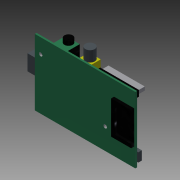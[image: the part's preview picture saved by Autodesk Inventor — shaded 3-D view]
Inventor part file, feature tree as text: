
AUTODESK INVENTOR PART (.ipt)
format: ipt  version: 2014 (Build 180170000, 170)  size: 240,128 bytes
history: native  units: mm
features: extrude x14, sketch x14
ambient origin geometry x8: Origin, YZ Plane, XZ Plane, XY Plane, X Axis, Y Axis, Z Axis, Center Point
bodies: Volumenkörper1 (feature_tree)
feature tree (28):
  extrude  "Extrusion1"  Depth=56.0mm
  extrude  "Extrusion2"  Depth=21.0mm
  extrude  "Extrusion3"  Depth=1.2mm
  extrude  "Extrusion4"  Depth=7.7mm
  extrude  "Extrusion5"  Depth=13.2mm
  extrude  "Extrusion6"  Depth=1.0mm
  extrude  "Extrusion7"  Depth=11.8mm
  extrude  "Extrusion8"  Depth=5.5mm TaperAngle=0.0deg
  extrude  "Extrusion9"  Depth=12.0mm
  extrude  "Extrusion10"  Depth=10.0mm TaperAngle=0.0deg
  extrude  "Extrusion11"  Depth=3.5mm
  extrude  "Extrusion12"  Depth=10.0mm
  extrude  "Extrusion13"  Depth=2.5mm
  extrude  "Extrusion14"  Depth=10.2mm TaperAngle=0.0deg
  sketch  "Skizze1"  dims[d0=85.0mm d1=56.0mm]
  sketch  "Skizze2"  dims[d2=1.5mm d3=0.0mm d4=21.0mm]
  sketch  "Skizze3"  dims[d5=16.0mm d6=1.2mm]
  sketch  "Skizze4"  dims[d7=13.4mm d8=0.0mm d9=7.7mm]
  sketch  "Skizze5"  dims[d10=17.2mm d11=13.2mm]
  sketch  "Skizze6"  dims[d13=16.0mm d14=0.0mm d15=1.0mm]
  sketch  "Skizze7"  dims[d16=15.0mm d17=11.8mm]
  sketch  "Skizze8"  dims[d18=15.0mm d19=5.5mm d20=0.0mm]
  sketch  "Skizze9"  dims[d21=11.5mm d22=12.0mm]
  sketch  "Skizze10"  dims[d23=14.5mm d24=10.0mm d25=0.0mm]
  sketch  "Skizze11"  dims[d26=7.0mm d27=3.5mm]
  sketch  "Skizze12"  dims[d28=3.5mm d29=0.0mm d30=10.0mm]
  sketch  "Skizze13"  dims[d31=10.0mm d32=2.5mm]
  sketch  "Skizze14"  dims[d33=7.5mm d34=10.2mm d35=0.0mm d36=8.0mm d37=0.0mm d38=9.0mm d39=0.0mm d40=32.7mm d41=5.0mm d42=1.0mm d43=1.0mm d44=2.5mm d45=0.0mm d50=1.0mm d51=1.0mm d52=1.0mm d53=1.0mm d54=6.0mm d55=0.0mm d56=1.0mm d57=7.5mm d58=5.6mm d59=4.0mm d60=3.0mm d61=0.0mm d62=15.5mm d63=17.0mm d64=28.0mm d65=1.0mm d66=0.5mm d67=0.0mm d69=24.0mm d70=3.0mm d71=3.0mm d72=45.0deg d73=19.0mm d74=2.0mm d75=0.0mm d76=2.9mm d77=25.5mm d78=18.0mm d79=2.9mm d80=5.0mm d81=12.5mm d82=2.0mm d83=0.0mm d84=1.0mm d85=18.8mm]
